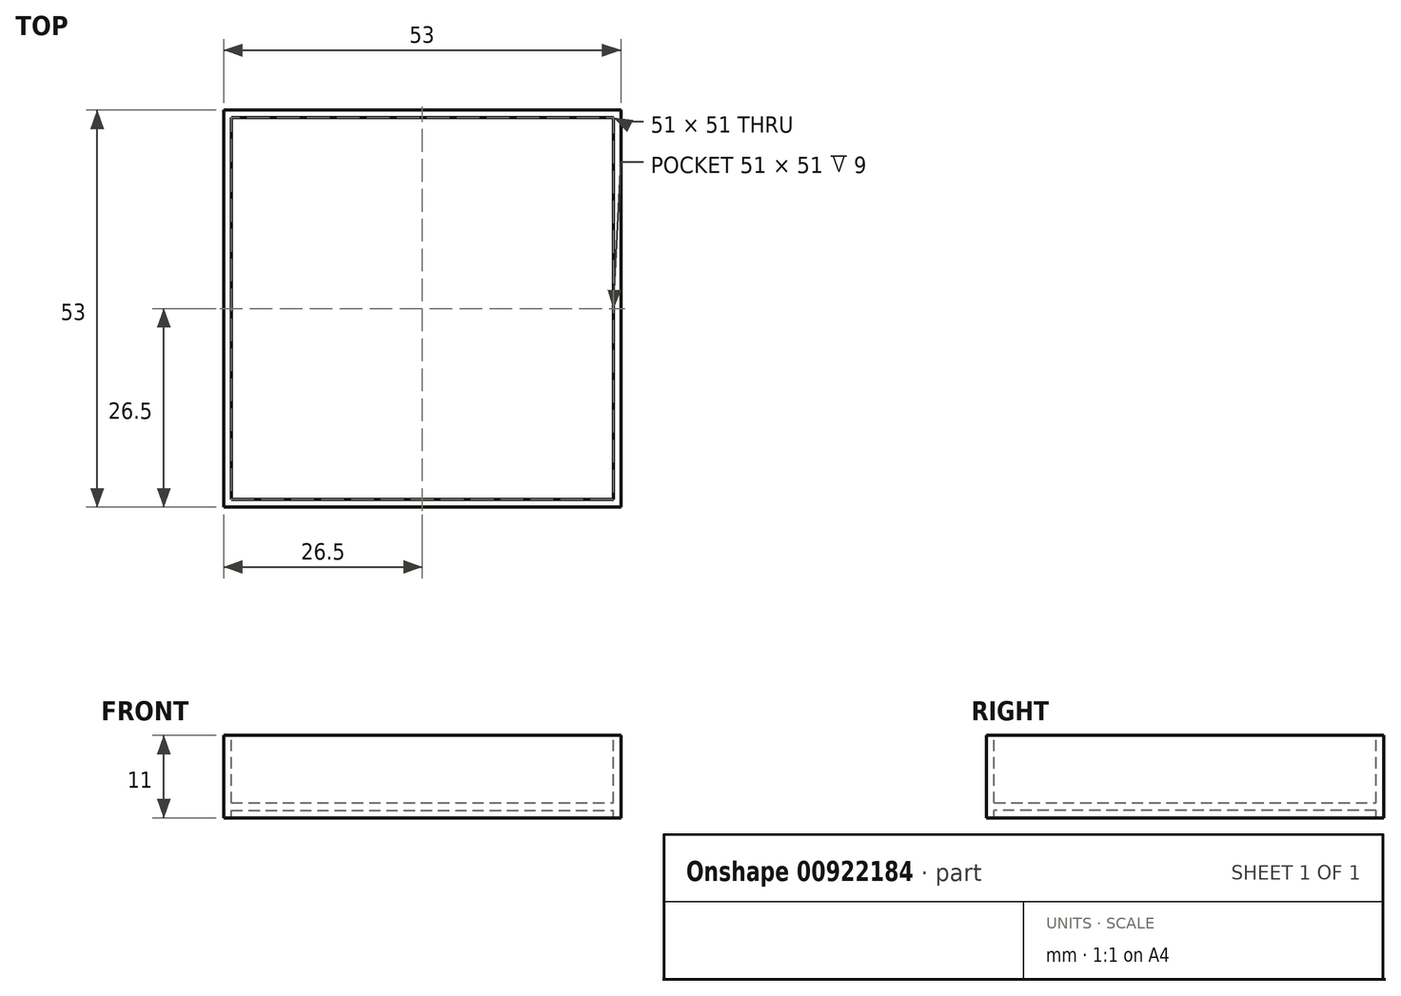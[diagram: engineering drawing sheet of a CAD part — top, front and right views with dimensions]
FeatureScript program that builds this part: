
annotation { "Feature Type Name" : "Feature", "Feature Type Description" : "" }
export const myFeature = defineFeature(function(context is Context, id is Id, definition is map)
    precondition{}
    {
        {
            var Q0;
            Q0=qCreatedBy(makeId("Top.planeOp"),FACE);
            var sketch = newSketch(context, id + "F0", { "sketchPlane" : qUnion([Q0])});
            skLineSegment(sketch, "E0.bottom", {"start": v(26.5, -26.5) * mm, "end": v(-26.5, -26.5) * mm});
            skLineSegment(sketch, "E0.top", {"start": v(26.5, 26.5) * mm, "end": v(-26.5, 26.5) * mm});
            skLineSegment(sketch, "E0.left", {"start": v(26.5, -26.5) * mm, "end": v(26.5, 26.5) * mm});
            skLineSegment(sketch, "E0.right", {"start": v(-26.5, -26.5) * mm, "end": v(-26.5, 26.5) * mm});
            skPoint(sketch, "E0.middle", {"position": v(0, 0) * mm});
            skSolve(sketch);
        }
        {
            var Q0;
            Q0=makeQuery(id+"F0.imprint","IMPRINT",FACE,{"disambiguationData":[TD([[makeQuery(id+"F0.imprint","IMPRINT",EDGE,{"derivedFrom":sQuery(id+"F0.wireOp",EDGE,"E0.bottom")}),-1.0]])]});
            extrude(context, id + "F1", {"entities" : qUnion([Q0]), "depth" : 10 * mm, "offsetDistance" : 25 * mm});
        }
        {
            var Q0;
            Q0=makeQuery(id+"F1.opExtrude","CAP_FACE",FACE,{"disambiguationData":[OSD([sQuery(id+"F0.wireOp",EDGE,"E0.bottom"),sQuery(id+"F0.wireOp",EDGE,"E0.top"),sQuery(id+"F0.wireOp",EDGE,"E0.left"),sQuery(id+"F0.wireOp",EDGE,"E0.right")])],"isStart":true});
            var sketch = newSketch(context, id + "F2", { "sketchPlane" : qUnion([Q0])});
            skLineSegment(sketch, "E1.0", {"start": v(25.5, -25.5) * mm, "end": v(25.5, 25.5) * mm});
            skLineSegment(sketch, "E1.1", {"start": v(-25.5, -25.5) * mm, "end": v(25.5, -25.5) * mm});
            skLineSegment(sketch, "E1.2", {"start": v(-25.5, 25.5) * mm, "end": v(-25.5, -25.5) * mm});
            skLineSegment(sketch, "E1.3", {"start": v(25.5, 25.5) * mm, "end": v(-25.5, 25.5) * mm});
            skSolve(sketch);
        }
        {
            var Q0;
            Q0=makeQuery(id+"F2.imprint","IMPRINT",FACE,{"disambiguationData":[TD([[makeQuery(id+"F2.imprint","IMPRINT",EDGE,{"derivedFrom":sQuery(id+"F2.wireOp",EDGE,"E1.0")}),-1.0]])]});
            extrude(context, id + "F3", {"entities" : qUnion([Q0]), "operationType" : NewBodyOperationType.ADD, "depth" : 1 * mm, "offsetDistance" : 25 * mm});
        }
        {
            var Q0;
            Q0=makeQuery(id+"F1.opExtrude","CAP_FACE",FACE,{"disambiguationData":[OSD([sQuery(id+"F0.wireOp",EDGE,"E0.bottom"),sQuery(id+"F0.wireOp",EDGE,"E0.top"),sQuery(id+"F0.wireOp",EDGE,"E0.left"),sQuery(id+"F0.wireOp",EDGE,"E0.right")])],"isStart":false});
            var sketch = newSketch(context, id + "F4", { "sketchPlane" : qUnion([Q0])});
            skLineSegment(sketch, "E2.0", {"start": v(25.5, -25.5) * mm, "end": v(25.5, 25.5) * mm});
            skLineSegment(sketch, "E2.1", {"start": v(-25.5, -25.5) * mm, "end": v(25.5, -25.5) * mm});
            skLineSegment(sketch, "E2.2", {"start": v(-25.5, 25.5) * mm, "end": v(-25.5, -25.5) * mm});
            skLineSegment(sketch, "E2.3", {"start": v(25.5, 25.5) * mm, "end": v(-25.5, 25.5) * mm});
            skSolve(sketch);
        }
        {
            var Q0;
            Q0=makeQuery(id+"F4.imprint","IMPRINT",FACE,{"disambiguationData":[TD([[makeQuery(id+"F4.imprint","IMPRINT",EDGE,{"derivedFrom":sQuery(id+"F4.wireOp",EDGE,"E2.0")}),1.0]])]});
            extrude(context, id + "F5", {"entities" : qUnion([Q0]), "operationType" : NewBodyOperationType.REMOVE, "oppositeDirection" : true, "depth" : 9 * mm, "offsetDistance" : 25 * mm});
        }
    });
